# Revit family: LINEAL 12W II ASIMETRICA_LKC0616WW_CW
name_source: partatom
category: Luminarias
units: mm (PartAtom-declared; Revit-internal decimal feet)

## family parameters
Compartido = No
Corte con vacíos al cargar = No
Cota de conector redondo = Diámetro de uso
Origen de luz = Sí
Punto de cálculo de habitación = No
Se basa en plano de trabajo = Sí
Siempre vertical = No
Tipo de pieza = Normal

## types (2) — shared parameters
Cambio de temperatura de color de luz atenuada = <Ninguno>
Comentarios de vataje = 100-240V
Fabricante = BRILLANT
Filtro de color = 16777215
Longitud de línea de emisión = 200 mm  [stored 0.656168 ft]
Lámpara = OSRAM
Watt per fixture = 12
Ángulo de inclinación = 30.00°
zero-valued in all types: Elevación por defecto

## per-type parameters (varying)
| type | Archivo de red fotométrica | Descripción | Modelo |
| EMP_LKC0616WW | LKC0616WW.IES | LUMINARIA PARA EMPOTRAR TIPO LINEAL CON 6 LED TIPO OSRAM CON UNA POTENCIA DE 12W, CUERPO DE ALUMINIO FUNDIDO A PRESION CUBIERTO CON POLVO GRIS OSCURO CON CUBIERTA DE ACERO INOXIDABLE Y VIDRIO TEMPLADO DE 8MM, PLACAS DE PVC PARA INSTALACION POR COLADO Y EVITAR DEFORMACIONES EN EL HOUSING (MATERIAL ABS), CON UNA DIMENSION DE 90MM DE PROFUNDO POR 328 DE LARGO EN LA LUMINARIA, CUENTA CON 733 LUMENES A UNA TEMPERATURA EN BLANCO CALIDO DE 3000K, CORRIENTE DE OPERACIÓN A 100mA, ON/OFF, DIMEABLE EN TRIAC O DALI (OPCIONAL), CABLE H05RN L0.5M, IRC 80, IK08, IP67, ANGULO DE APERTURA ASIMETRICA A 45X35 GRADOS EN STOCK, ALIMENTADA A 100-240V. | LKC0616WW |
| EMP_LKC0616CW | generic | LUMINARIA PARA EMPOTRAR TIPO LINEAL CON 6 LED TIPO OSRAM CON UNA POTENCIA DE 12W, CUERPO DE ALUMINIO FUNDIDO A PRESION CUBIERTO CON POLVO GRIS OSCURO CON CUBIERTA DE ACERO INOXIDABLE Y VIDRIO TEMPLADO DE 8MM, PLACAS DE PVC PARA INSTALACION POR COLADO Y EVITAR DEFORMACIONES EN EL HOUSING (MATERIAL ABS), CON UNA DIMENSION DE 90MM DE PROFUNDO POR 328 DE LARGO EN LA LUMINARIA, CUENTA CON 1100 LUMENES A UNA TEMPERATURA EN BLANCO FRIO DE 6000K, CORRIENTE DE OPERACIÓN A 100mA, ON/OFF, DIMEABLE EN TRIAC O DALI (OPCIONAL), CABLE H05RN L0.5M, IRC 80, IK08, IP67, ANGULO DE APERTURA ASIMETRICA A 45X35 GRADOS EN STOCK, ALIMENTADA A 100-240V. | LKC0616CW |

note: [stored X ft] marks values corroborated as IEEE doubles in the binary element streams (Revit-internal decimal feet)

## geometry (parser evidence)
native form markers: Blend x2
no freeform markers — native parametric forms only
